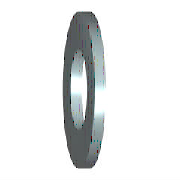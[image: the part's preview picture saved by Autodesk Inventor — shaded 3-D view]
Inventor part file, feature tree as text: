
AUTODESK INVENTOR PART (.ipt)
format: ipt  version: 2024.2 (Build 282272000, 272)  size: 110,080 bytes
history: native  units: mm (DEFAULTED — no unit token found)
features: other x1, plane x1
ambient origin geometry x7: Origin, YZ Plane, XY Plane, X Axis, Y Axis, Z Axis, Center Point
bodies: Solid1 (feature_tree), Body (feature_tree)
feature tree (2):
  other  "Work Axis1"
  plane  "Work Plane1"
